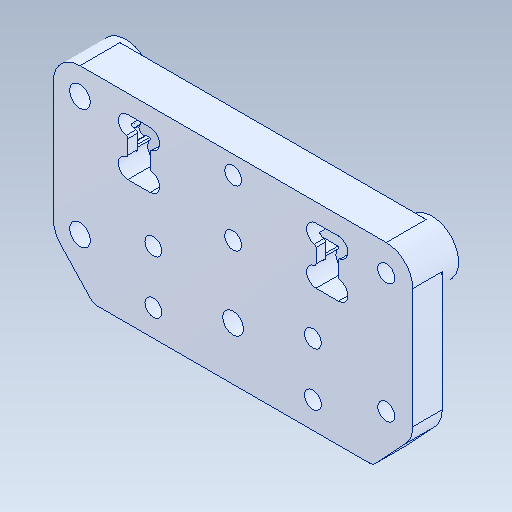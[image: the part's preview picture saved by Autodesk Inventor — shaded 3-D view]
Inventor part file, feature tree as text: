
AUTODESK INVENTOR PART (.ipt)
format: ipt  version: 2020 (Build 240168000, 168)  size: 218,624 bytes
history: native  units: in
note: dims shown in document units (in); Inventor stores cm internally (conversion verified against a paired STEP export)
features: fillet x1
ambient origin geometry x8: Origin, YZ Plane, XZ Plane, XY Plane, X Axis, Y Axis, Z Axis, Center Point
bodies: Solid1 (feature_tree)
feature tree (1):
  fillet  "Fillet10"  [1 undecoded]
note: 1 required parameter value undecoded (feature->parameter linkage not recoverable at this tier; creation-order binding heuristic only, values carry confidence <= 0.55)
